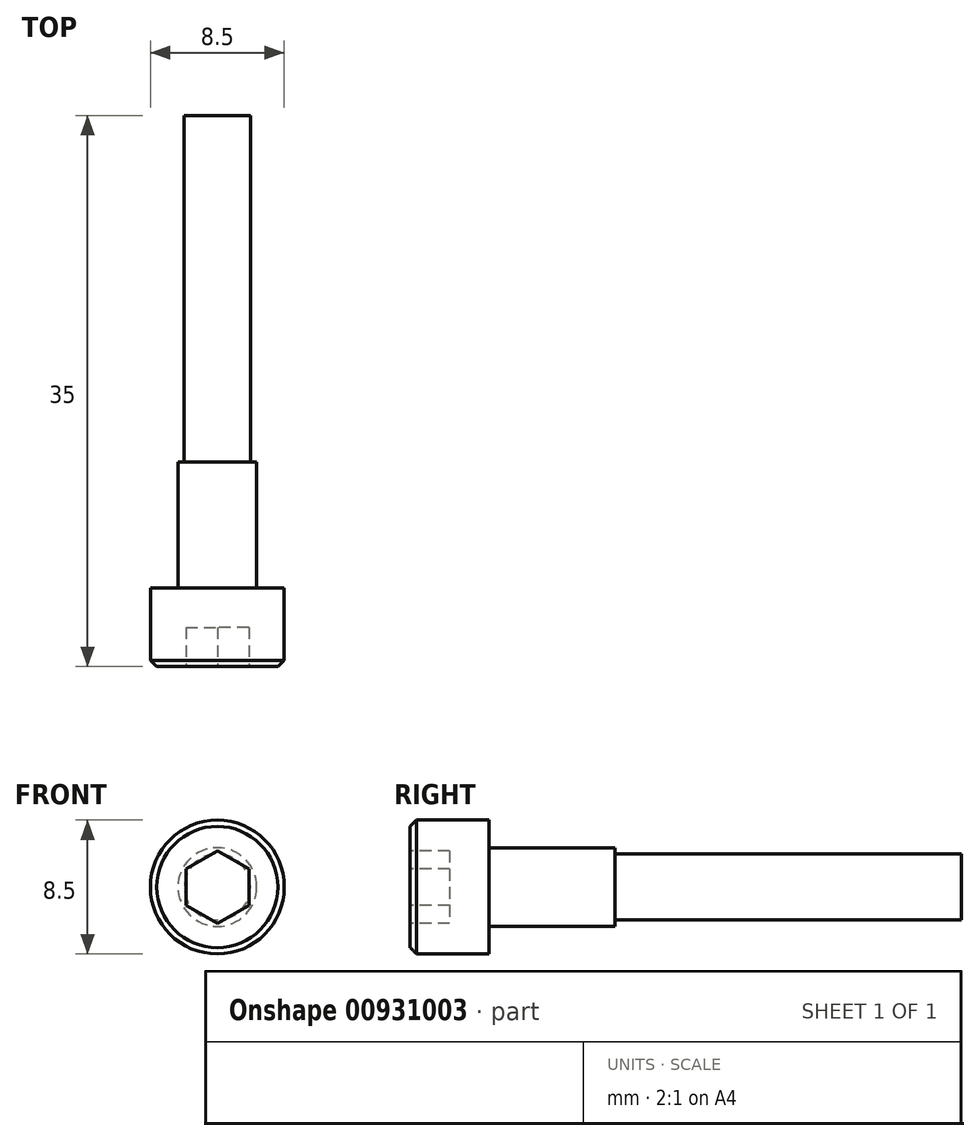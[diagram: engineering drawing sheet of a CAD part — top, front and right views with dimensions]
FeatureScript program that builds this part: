
annotation { "Feature Type Name" : "Feature", "Feature Type Description" : "" }
export const myFeature = defineFeature(function(context is Context, id is Id, definition is map)
    precondition{}
    {
        {
            var Q0;
            Q0=qCreatedBy(makeId("Front.planeOp"),FACE);
            var sketch = newSketch(context, id + "F0", { "sketchPlane" : qUnion([Q0])});
            skCircle(sketch, "E0", {"center": v(0, 0) * mm, "radius": 4.25 * mm});
            skSolve(sketch);
        }
        {
            var Q0;
            Q0=makeQuery(id+"F0.imprint","IMPRINT",FACE,{"disambiguationData":[TD([[makeQuery(id+"F0.imprint","IMPRINT",EDGE,{"derivedFrom":sQuery(id+"F0.wireOp",EDGE,"E0")}),1.0]])]});
            extrude(context, id + "F1", {"entities" : qUnion([Q0]), "depth" : 5 * mm, "offsetDistance" : 25 * mm});
        }
        {
            var Q0;
            Q0=makeQuery(id+"F1.opExtrude","CAP_FACE",FACE,{"disambiguationData":[OSD([sQuery(id+"F0.wireOp",EDGE,"E0")])],"isStart":true});
            var sketch = newSketch(context, id + "F2", { "sketchPlane" : qUnion([Q0])});
            skCircle(sketch, "E1", {"center": v(0, 0) * mm, "radius": 2.5 * mm});
            skSolve(sketch);
        }
        {
            var Q0;
            Q0=makeQuery(id+"F2.imprint","IMPRINT",FACE,{"disambiguationData":[TD([[makeQuery(id+"F2.imprint","IMPRINT",EDGE,{"derivedFrom":sQuery(id+"F2.wireOp",EDGE,"E1")}),1.0]])]});
            extrude(context, id + "F3", {"entities" : qUnion([Q0]), "operationType" : NewBodyOperationType.ADD, "depth" : 30 * mm, "offsetDistance" : 25 * mm});
        }
        {
            var Q0;
            Q0=makeQuery(id+"F3.opExtrude","CAP_FACE",FACE,{"disambiguationData":[OSD([sQuery(id+"F2.wireOp",EDGE,"E1")])],"isStart":false});
            var sketch = newSketch(context, id + "F4", { "sketchPlane" : qUnion([Q0])});
            skCircle(sketch, "E2", {"center": v(0, 0) * mm, "radius": 2.1 * mm});
            skSolve(sketch);
        }
        {
            var Q0;
            Q0=makeQuery(id+"F4.imprint","IMPRINT",FACE,{"disambiguationData":[TD([[makeQuery(id+"F4.imprint","IMPRINT",EDGE,{"derivedFrom":sQuery(id+"F4.wireOp",EDGE,"E2")}),-1.0]])]});
            extrude(context, id + "F5", {"entities" : qUnion([Q0]), "operationType" : NewBodyOperationType.REMOVE, "oppositeDirection" : true, "depth" : 22 * mm, "offsetDistance" : 25 * mm});
        }
        {
            var Q0;
            Q0=makeQuery(id+"F1.opExtrude","CAP_FACE",FACE,{"disambiguationData":[OSD([sQuery(id+"F0.wireOp",EDGE,"E0")])],"isStart":false});
            var sketch = newSketch(context, id + "F6", { "sketchPlane" : qUnion([Q0])});
            skCircle(sketch, "E3.cCircle", {"center": v(0, 0) * mm, "radius": 2 * mm, "construction": true});
            skLineSegment(sketch, "E3.0", {"start": v(2, -1.15) * mm, "end": v(0, -2.3) * mm});
            skLineSegment(sketch, "E3.1", {"start": v(0, -2.3) * mm, "end": v(-2, -1.15) * mm});
            skLineSegment(sketch, "E3.2", {"start": v(-2, -1.15) * mm, "end": v(-2, 1.15) * mm});
            skLineSegment(sketch, "E3.3", {"start": v(-2, 1.15) * mm, "end": v(0, 2.3) * mm});
            skLineSegment(sketch, "E3.4", {"start": v(0, 2.3) * mm, "end": v(2, 1.15) * mm});
            skLineSegment(sketch, "E3.5", {"start": v(2, 1.15) * mm, "end": v(2, -1.15) * mm});
            skPoint(sketch, "E3.0.midPoint", {"position": v(1, -1.73) * mm});
            skLineSegment(sketch, "E4", {"start": v(0, 0) * mm, "end": v(4.25, 0) * mm, "construction": true});
            skSolve(sketch);
        }
        {
            var Q0;
            Q0=qSketchRegion(id+"F6",true);
            extrude(context, id + "F7", {"entities" : qUnion([Q0]), "operationType" : NewBodyOperationType.REMOVE, "oppositeDirection" : true, "depth" : 2.5 * mm, "offsetDistance" : 25 * mm});
        }
        {
            var Q0;
            Q0=makeQuery(id+"F1.opExtrude","CAP_EDGE",EDGE,{"disambiguationData":[OSD([sQuery(id+"F0.wireOp",EDGE,"E0")])],"isStart":false});
            chamfer(context, id + "F8", {"entities" : qUnion([Q0]), "width" : 0.4 * mm, "tangentPropagation" : true});
        }
    });
